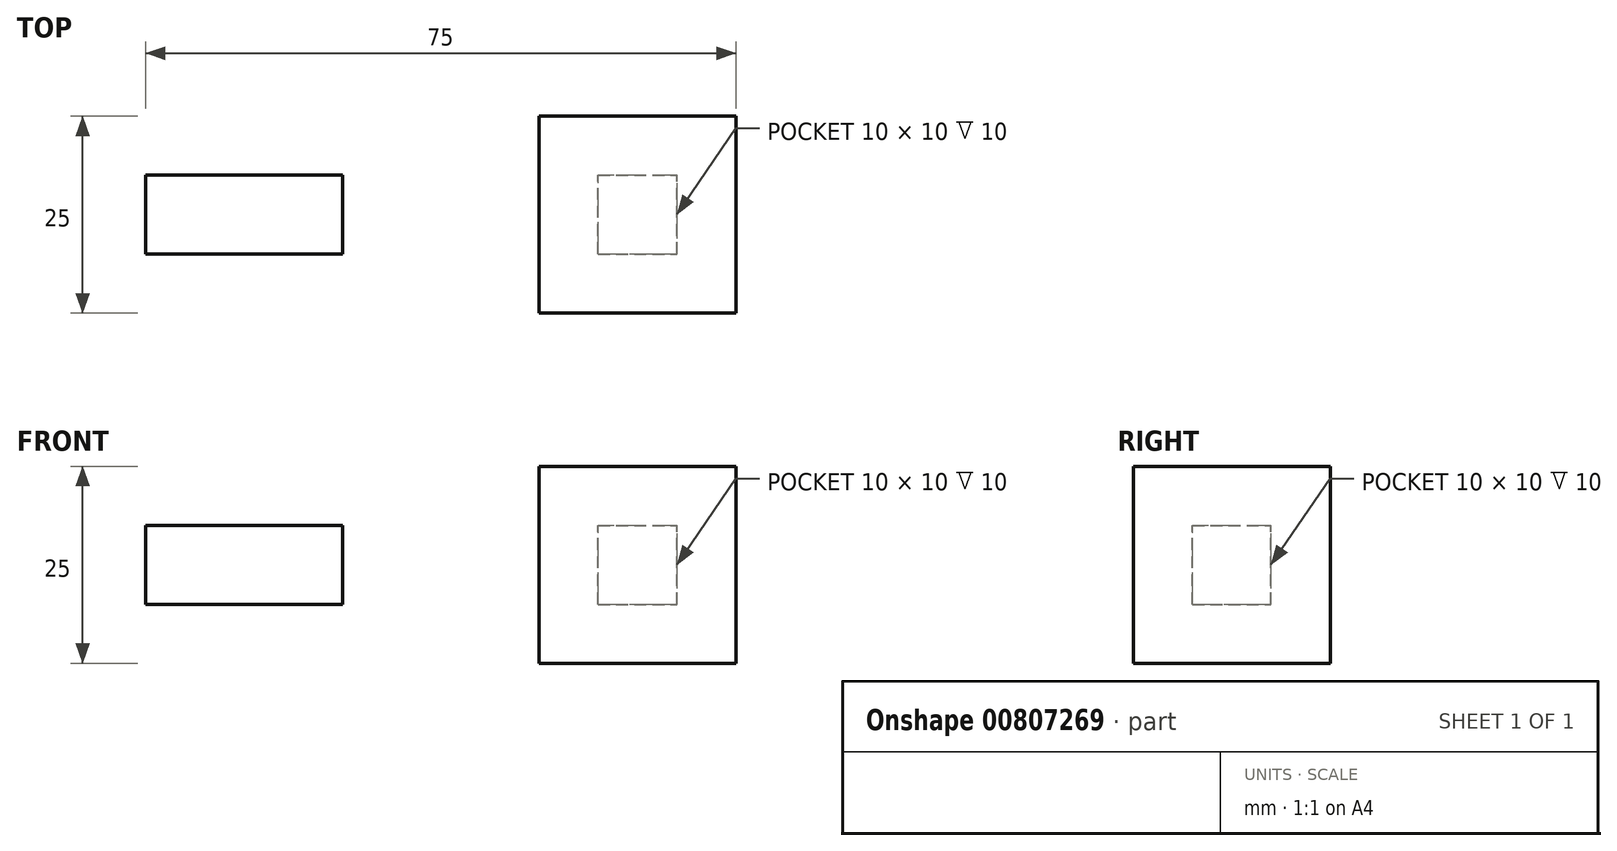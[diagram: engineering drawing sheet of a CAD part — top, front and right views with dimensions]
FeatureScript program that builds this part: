
annotation { "Feature Type Name" : "Feature", "Feature Type Description" : "" }
export const myFeature = defineFeature(function(context is Context, id is Id, definition is map)
    precondition{}
    {
        {
            var Q0;
            Q0=qCreatedBy(makeId("Front.planeOp"),FACE);
            var sketch = newSketch(context, id + "F0", { "sketchPlane" : qUnion([Q0])});
            skLineSegment(sketch, "E0.bottom", {"start": v(0, 0) * mm, "end": v(-25, 0) * mm});
            skLineSegment(sketch, "E0.top", {"start": v(0, 25) * mm, "end": v(-25, 25) * mm});
            skLineSegment(sketch, "E0.left", {"start": v(0, 0) * mm, "end": v(0, 25) * mm});
            skLineSegment(sketch, "E0.right", {"start": v(-25, 0) * mm, "end": v(-25, 25) * mm});
            skSolve(sketch);
        }
        {
            var Q0;
            Q0=makeQuery(id+"F0.imprint","IMPRINT",FACE,{"disambiguationData":[TD([[makeQuery(id+"F0.imprint","IMPRINT",EDGE,{"derivedFrom":sQuery(id+"F0.wireOp",EDGE,"E0.bottom")}),-1.0]])]});
            extrude(context, id + "F1", {"entities" : qUnion([Q0]), "depth" : 25 * mm, "offsetDistance" : 25 * mm});
        }
        {
            var Q0;
            Q0=makeQuery(id+"F1.opExtrude","SWEPT_FACE",FACE,{"disambiguationData":[OSD([sQuery(id+"F0.wireOp",EDGE,"E0.left")])]});
            cPlane(context, id + "F2", {"entities" : qUnion([Q0]), "cplaneType" : CPlaneType.OFFSET, "offset" : 25 * mm, "width" : 150 * mm, "height" : 150 * mm});
        }
        {
            var Q0;
            Q0=qCreatedBy(id+"F2.planeOp",FACE);
            var sketch = newSketch(context, id + "F3", { "sketchPlane" : qUnion([Q0])});
            skLineSegment(sketch, "E1.bottom", {"start": v(-17.5, 7.5) * mm, "end": v(-7.5, 7.5) * mm});
            skLineSegment(sketch, "E1.top", {"start": v(-17.5, 17.5) * mm, "end": v(-7.5, 17.5) * mm});
            skLineSegment(sketch, "E1.left", {"start": v(-17.5, 7.5) * mm, "end": v(-17.5, 17.5) * mm});
            skLineSegment(sketch, "E1.right", {"start": v(-7.5, 7.5) * mm, "end": v(-7.5, 17.5) * mm});
            skSolve(sketch);
        }
        {
            var Q0;
            Q0=makeQuery(id+"F3.imprint","IMPRINT",FACE,{"disambiguationData":[TD([[makeQuery(id+"F3.imprint","IMPRINT",EDGE,{"derivedFrom":sQuery(id+"F3.wireOp",EDGE,"E1.bottom")}),1.0]])]});
            extrude(context, id + "F4", {"entities" : qUnion([Q0]), "operationType" : NewBodyOperationType.REMOVE, "oppositeDirection" : true, "depth" : (50 - 7.5) * mm, "offsetDistance" : 25 * mm, "hasSecondDirection" : true, "secondDirectionOppositeDirection" : true, "secondDirectionDepth" : (25 + 7.5) * mm});
        }
        {
            var Q0;
            Q0=makeQuery(id+"F3.imprint","IMPRINT",FACE,{"disambiguationData":[TD([[makeQuery(id+"F3.imprint","IMPRINT",EDGE,{"derivedFrom":sQuery(id+"F3.wireOp",EDGE,"E1.bottom")}),1.0]])]});
            extrude(context, id + "F5", {"entities" : qUnion([Q0]), "oppositeDirection" : true, "depth" : 100 * mm, "offsetDistance" : 25 * mm, "hasSecondDirection" : true, "secondDirectionOppositeDirection" : true, "secondDirectionDepth" : 75 * mm});
        }
    });
